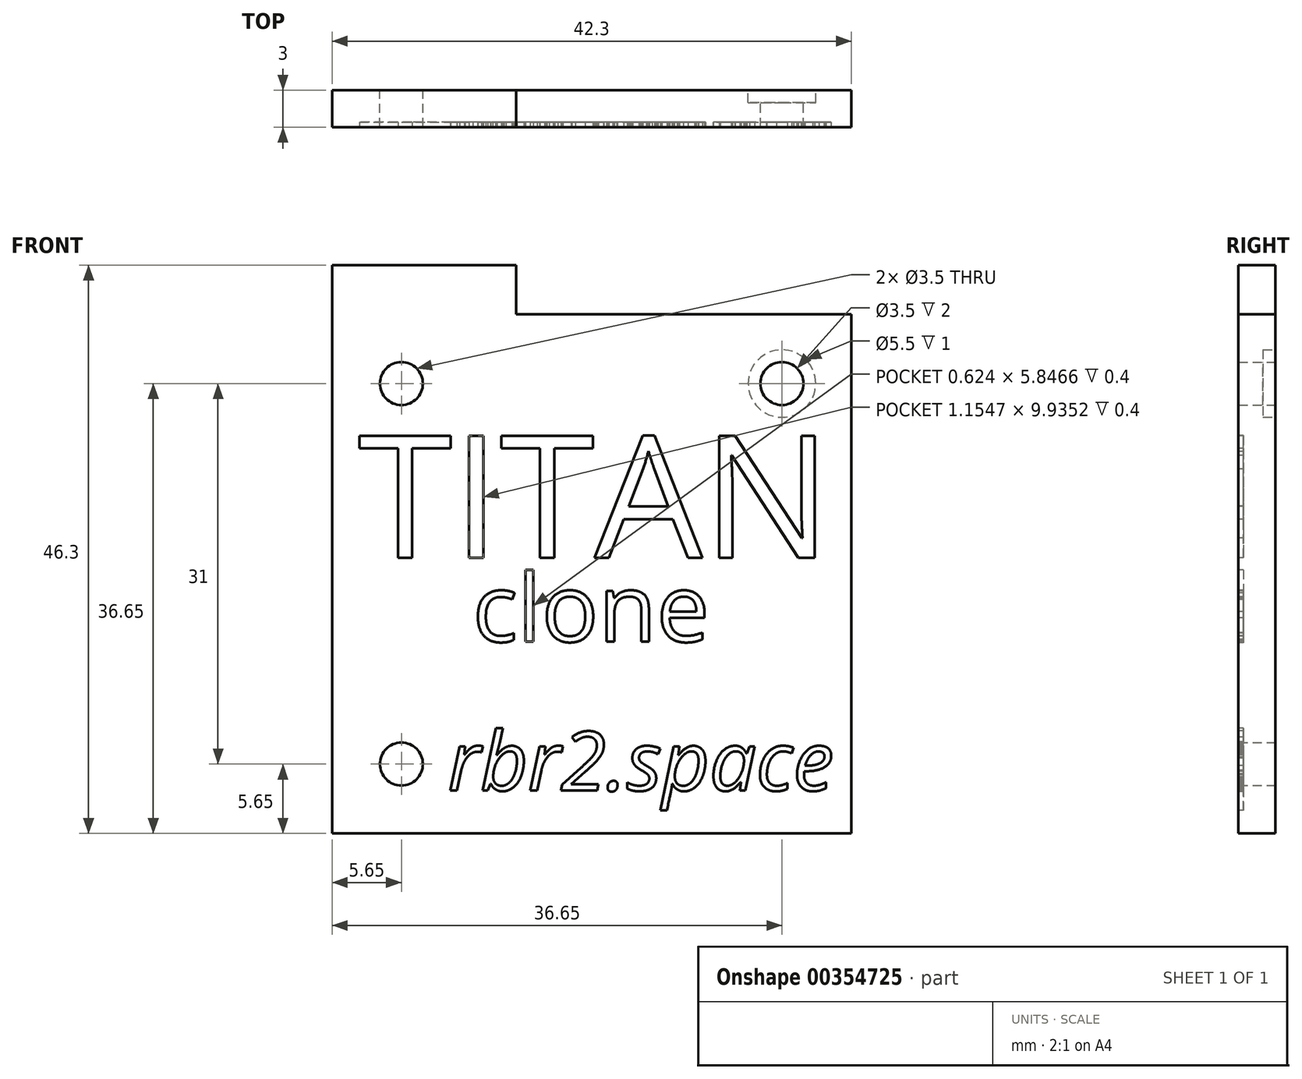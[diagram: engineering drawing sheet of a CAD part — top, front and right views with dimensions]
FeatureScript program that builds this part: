
annotation { "Feature Type Name" : "Feature", "Feature Type Description" : "" }
export const myFeature = defineFeature(function(context is Context, id is Id, definition is map)
    precondition{}
    {
        {
            var Q0;
            Q0=qCreatedBy(makeId("Front.planeOp"),FACE);
            var sketch = newSketch(context, id + "F0", { "sketchPlane" : qUnion([Q0])});
            skLineSegment(sketch, "E0.bottom", {"start": v(21.15, 21.15) * mm, "end": v(-21.15, 21.15) * mm});
            skLineSegment(sketch, "E0.top", {"start": v(21.15, -21.15) * mm, "end": v(-21.15, -21.15) * mm});
            skLineSegment(sketch, "E0.left", {"start": v(21.15, 21.15) * mm, "end": v(21.15, -21.15) * mm});
            skLineSegment(sketch, "E0.right", {"start": v(-21.15, 21.15) * mm, "end": v(-21.15, -21.15) * mm});
            skPoint(sketch, "E0.middle", {"position": v(0, 0) * mm});
            skCircle(sketch, "E1", {"center": v(-15.5, 15.5) * mm, "radius": 1.75 * mm});
            skCircle(sketch, "E2.MirrorC", {"center": v(15.5, 15.5) * mm, "radius": 1.75 * mm});
            skCircle(sketch, "E3.MirrorC", {"center": v(-15.5, -15.5) * mm, "radius": 1.75 * mm});
            skCircle(sketch, "E4.MirrorC", {"center": v(15.5, -15.5) * mm, "radius": 1.75 * mm, "construction": true});
            skCircle(sketch, "E5", {"center": v(0, 0) * mm, "radius": 3 * mm, "construction": true});
            skLineSegment(sketch, "E6", {"start": v(-21.15, 21.15) * mm, "end": v(-21.15, 25.15) * mm});
            skLineSegment(sketch, "E7", {"start": v(-21.15, 25.15) * mm, "end": v(-6.15, 25.15) * mm});
            skLineSegment(sketch, "E8", {"start": v(-6.15, 25.15) * mm, "end": v(-6.15, 21.15) * mm});
            skSolve(sketch);
        }
        {
            var Q0;
            Q0=qSketchRegion(id+"F0",true);
            extrude(context, id + "F1", {"entities" : qUnion([Q0]), "depth" : 3 * mm});
        }
        {
            var Q0;
            Q0=makeQuery(id+"F1.opExtrude","CAP_FACE",FACE,{"disambiguationData":[OSD([sQuery(id+"F0.wireOp",EDGE,"E0.bottom"),sQuery(id+"F0.wireOp",EDGE,"E0.top"),sQuery(id+"F0.wireOp",EDGE,"E0.left"),sQuery(id+"F0.wireOp",EDGE,"E0.right"),sQuery(id+"F0.wireOp",EDGE,"E1"),sQuery(id+"F0.wireOp",EDGE,"E2.MirrorC"),sQuery(id+"F0.wireOp",EDGE,"E3.MirrorC"),sQuery(id+"F0.wireOp",EDGE,"E6"),sQuery(id+"F0.wireOp",EDGE,"E7"),sQuery(id+"F0.wireOp",EDGE,"E8")])],"isStart":true});
            var sketch = newSketch(context, id + "F2", { "sketchPlane" : qUnion([Q0])});
            skCircle(sketch, "E9", {"center": v(-15.5, 15.5) * mm, "radius": 2.75 * mm});
            skSolve(sketch);
        }
        {
            var Q0;
            Q0=makeQuery(id+"F2.imprint","IMPRINT",FACE,{"disambiguationData":[TD([[makeQuery(id+"F2.imprint","IMPRINT",EDGE,{"derivedFrom":sQuery(id+"F2.wireOp",EDGE,"E9")}),1.0]])]});
            extrude(context, id + "F3", {"entities" : qUnion([Q0]), "operationType" : NewBodyOperationType.REMOVE, "oppositeDirection" : true, "depth" : 1 * mm});
        }
        {
            var Q0;
            Q0=makeQuery(id+"F1.opExtrude","CAP_FACE",FACE,{"disambiguationData":[OSD([sQuery(id+"F0.wireOp",EDGE,"E0.bottom"),sQuery(id+"F0.wireOp",EDGE,"E0.top"),sQuery(id+"F0.wireOp",EDGE,"E0.left"),sQuery(id+"F0.wireOp",EDGE,"E0.right"),sQuery(id+"F0.wireOp",EDGE,"E1"),sQuery(id+"F0.wireOp",EDGE,"E2.MirrorC"),sQuery(id+"F0.wireOp",EDGE,"E3.MirrorC"),sQuery(id+"F0.wireOp",EDGE,"E6"),sQuery(id+"F0.wireOp",EDGE,"E7"),sQuery(id+"F0.wireOp",EDGE,"E8")])],"isStart":false});
            var sketch = newSketch(context, id + "F4", { "sketchPlane" : qUnion([Q0])});
            skText(sketch, "E10", { "text": "TITAN", "fontName": "OpenSans-Regular.ttf"});
            skLineSegment(sketch, "E11", {"start": v(0, -6.08) * mm, "end": v(0, 23.24) * mm, "construction": true});
            skText(sketch, "E12", { "text": "clone", "fontName": "OpenSans-Regular.ttf"});
            skText(sketch, "E13", { "text": "rbr2.space", "fontName": "OpenSans-Italic.ttf"});
            const initialGuessF4  = {"E10": [-0.01905, 0.0013, 1, 0, 0.01002], "E12": [-0.0097, -0.00553, 1, 0, 0.00554], "E13": [-0.01172, -0.01766, 1, 0, 0.00483]};
            skSetInitialGuess(sketch, initialGuessF4);
            skSolve(sketch);
        }
        {
            var Q0;
            Q0=qSketchRegion(id+"F4",true);
            extrude(context, id + "F5", {"entities" : qUnion([Q0]), "operationType" : NewBodyOperationType.REMOVE, "oppositeDirection" : true, "depth" : .4 * mm});
        }
    });
